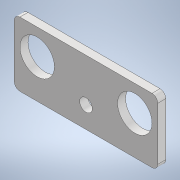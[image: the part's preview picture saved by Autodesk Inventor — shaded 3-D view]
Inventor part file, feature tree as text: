
AUTODESK INVENTOR PART (.ipt)
format: ipt  version: 2022.3 (Build 263350000, 350)  size: 190,464 bytes
history: native  units: mm
features: extrude x5, sketch x5, projected_geometry x4, other x3, fillet x1, reference x1
ambient origin geometry x8: Origin, YZ Plane, XZ Plane, XY Plane, X Axis, Y Axis, Z Axis, Center Point
bodies: Solid1 (feature_tree)
feature tree (19):
  extrude  "Extrusion1"  Depth=25.0mm
  extrude  "Extrusion2"  Depth=1.0mm
  extrude  "Extrusion3"  Depth=1.0mm
  fillet  "Fillet1"  Radius=6.0mm
  extrude  "Extrusion4"  Depth=10.0mm
  extrude  "Extrusion5"  Depth=1.0mm
  sketch  "Sketch1"  dims[d0=25.0mm d1=25.0mm]
  sketch  "Sketch3"  dims[d2=1.0mm d3=1.0mm]
  projected_geometry  "Projected Loop2"
  reference  "Reference1"
  sketch  "Sketch4"  dims[d4=1.0mm d5=1.0mm d6=6.0mm]
  projected_geometry  "Projected Loop3"
  sketch  "Sketch5"  dims[d7=6.0mm d8=10.0mm]
  projected_geometry  "Projected Loop4"
  sketch  "Sketch6"  dims[d9=1.3mm d10=2.0mm d11=1.0mm d12=0.0mm d13=1.0mm d14=0.0mm d15=1.0mm d16=0.0mm d17=1.0mm d18=0.2mm d19=0.0mm d20=0.2mm d21=0.0mm]
  projected_geometry  "Projected Loop5"
  other  "<userpath>\Documents\Inventor\NanoSumo\NanoSumo_part1.iam"
  other  "NanoSumo_part1.iam"
  other  "srodek:1"
